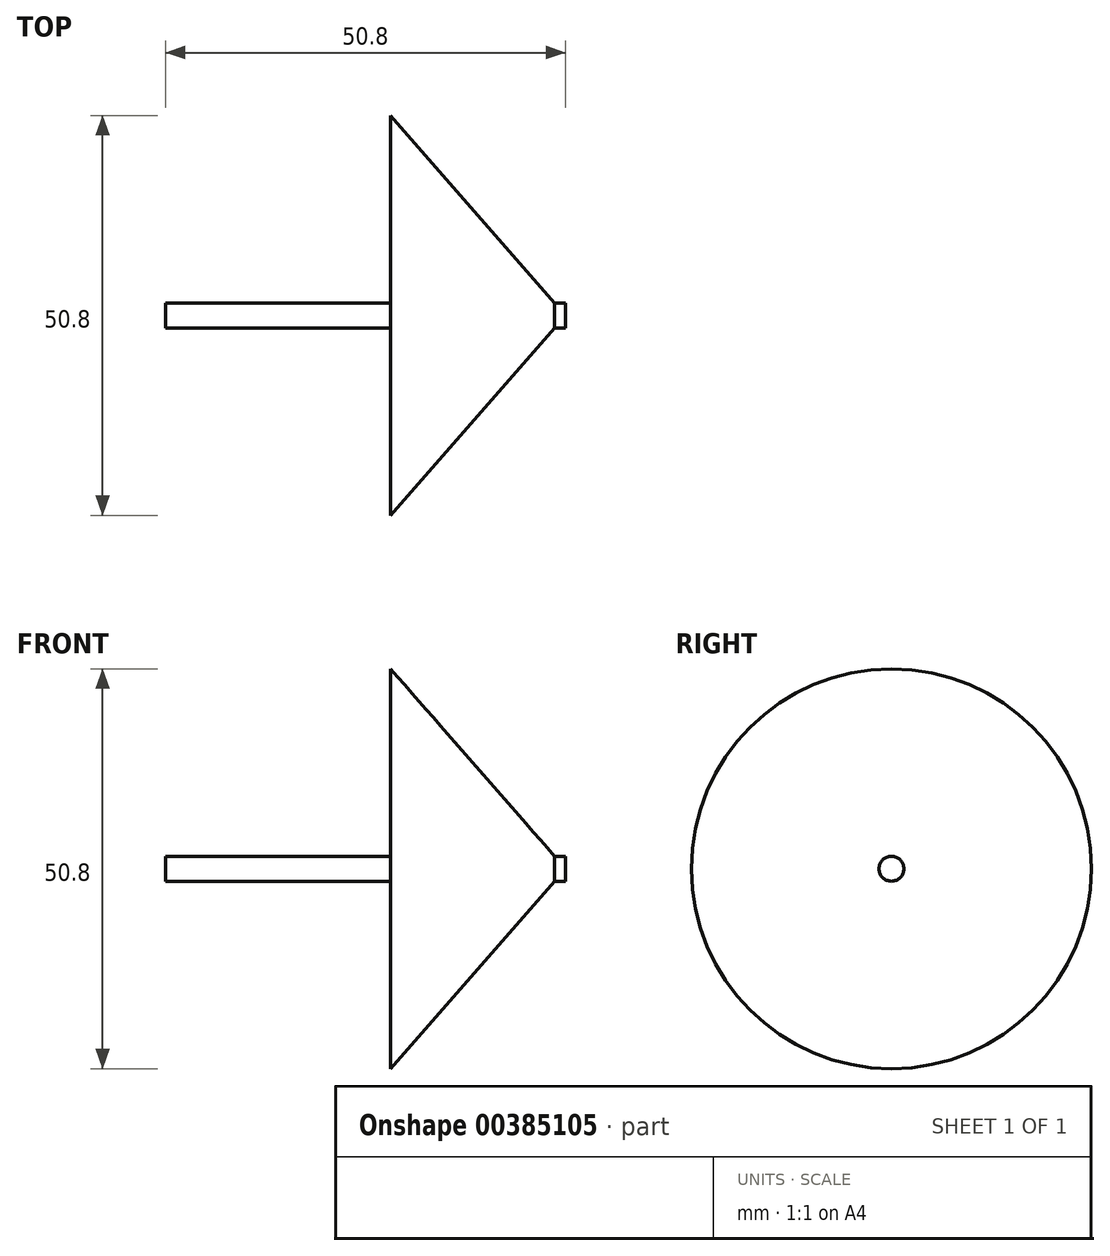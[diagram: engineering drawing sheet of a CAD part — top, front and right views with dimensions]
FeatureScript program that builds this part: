
annotation { "Feature Type Name" : "Feature", "Feature Type Description" : "" }
export const myFeature = defineFeature(function(context is Context, id is Id, definition is map)
    precondition{}
    {
        {
            var Q0;
            Q0=qCreatedBy(makeId("Top.planeOp"),FACE);
            var sketch = newSketch(context, id + "F0", { "sketchPlane" : qUnion([Q0])});
            skLineSegment(sketch, "E0", {"start": v(0, 0) * mm, "end": v(0, 1.59) * mm});
            skLineSegment(sketch, "E1", {"start": v(0, 1.59) * mm, "end": v(50.8, 1.59) * mm});
            skLineSegment(sketch, "E2", {"start": v(50.8, 1.59) * mm, "end": v(50.8, 0) * mm});
            skLineSegment(sketch, "E3", {"start": v(50.8, 0) * mm, "end": v(0, 0) * mm});
            skLineSegment(sketch, "E4", {"start": v(0, 1.59) * mm, "end": v(0, 0) * mm});
            skSolve(sketch);
        }
        {
            var Q0;
            Q0 = qSketchRegion(id + "F0", true);
            var Q1;
            Q1=sQuery(id+"F0.wireOp",EDGE,"E3");
            revolve(context, id + "F1", {"entities" : qUnion([Q0]), "axis" : qUnion([Q1]), "revolveType" : RevolveType.FULL});
        }
        {
            var Q0;
            Q0=qCreatedBy(makeId("Front.planeOp"),FACE);
            var sketch = newSketch(context, id + "F2", { "sketchPlane" : qUnion([Q0])});
            skLineSegment(sketch, "E5", {"start": v(28.58, 0) * mm, "end": v(28.58, 25.4) * mm});
            skLineSegment(sketch, "E6", {"start": v(28.57, 25.4) * mm, "end": v(50.8, 0) * mm});
            skLineSegment(sketch, "E7", {"start": v(50.8, 0) * mm, "end": v(28.58, 0) * mm});
            skSolve(sketch);
        }
        {
            var Q0;
            Q0=makeQuery(id+"F2.imprint","IMPRINT",FACE,{"disambiguationData":[TD([[makeQuery(id+"F2.imprint","IMPRINT",EDGE,{"derivedFrom":sQuery(id+"F2.wireOp",EDGE,"E5")}),-1.0]])]});
            var Q1;
            Q1=sQuery(id+"F2.wireOp",EDGE,"E7");
            revolve(context, id + "F3", {"operationType" : NewBodyOperationType.ADD, "entities" : qUnion([Q0]), "axis" : qUnion([Q1]), "revolveType" : RevolveType.FULL});
        }
    });
